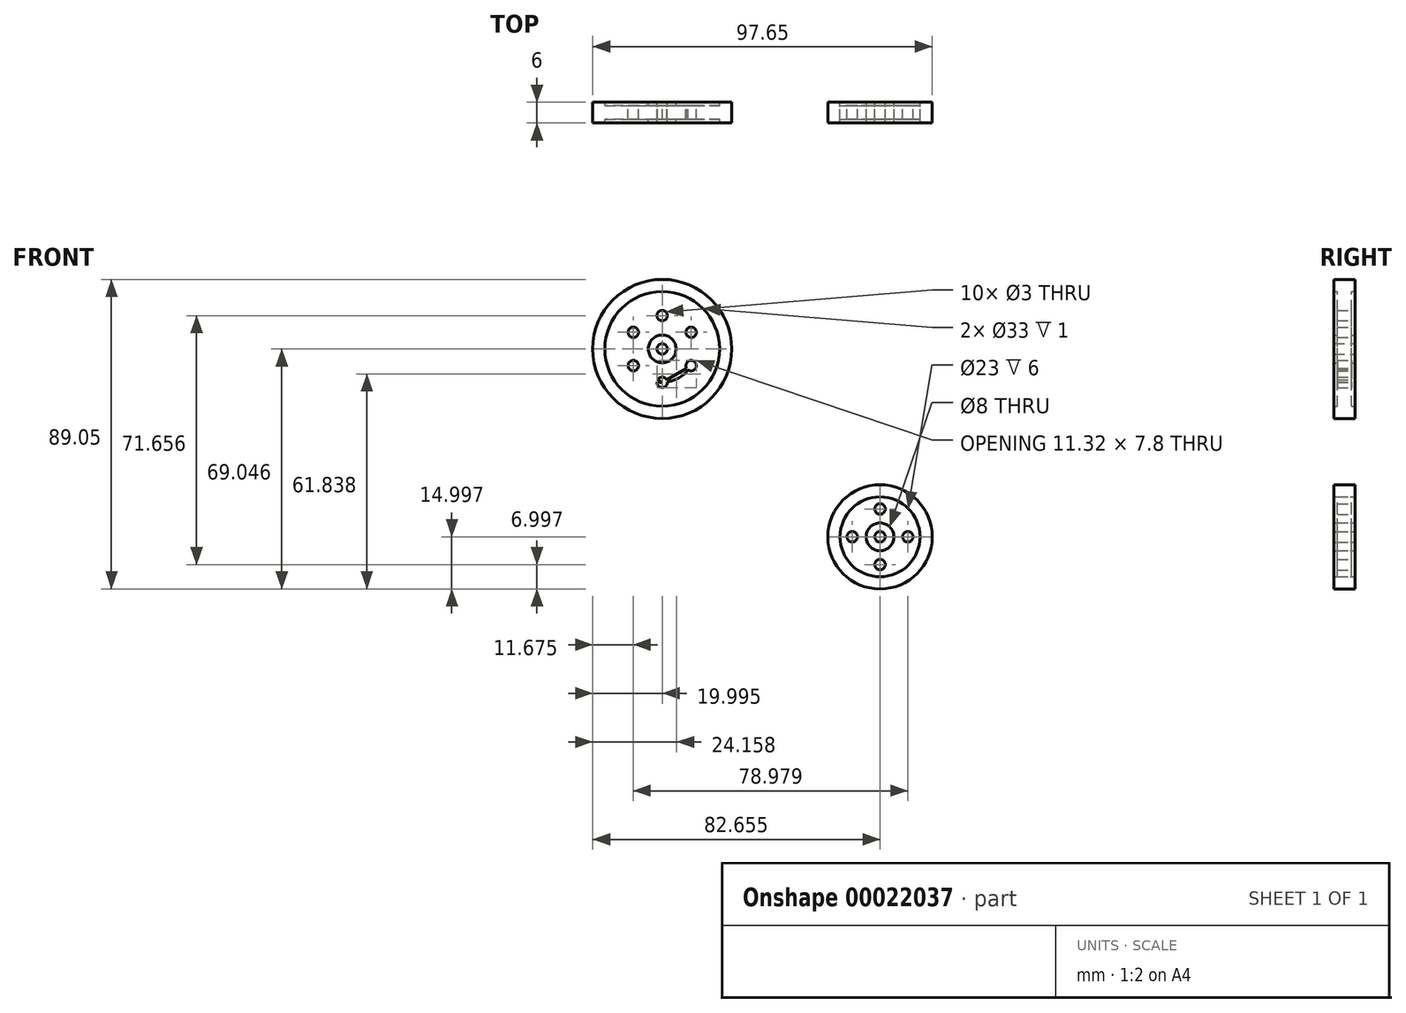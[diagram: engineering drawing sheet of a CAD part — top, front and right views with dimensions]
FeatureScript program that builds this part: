
annotation { "Feature Type Name" : "Feature", "Feature Type Description" : "" }
export const myFeature = defineFeature(function(context is Context, id is Id, definition is map)
    precondition{}
    {
        {
            var Q0;
            Q0=qCreatedBy(makeId("Front.planeOp"),FACE);
            var sketch = newSketch(context, id + "F0", { "sketchPlane" : qUnion([Q0])});
            skCircle(sketch, "E0", {"center": v(-77.4, 40.17) * mm, "radius": 20 * mm});
            skCircle(sketch, "E1", {"center": v(-77.4, 40.17) * mm, "radius": 4 * mm});
            skCircle(sketch, "E2", {"center": v(-77.4, 40.17) * mm, "radius": 9.6 * mm});
            skCircle(sketch, "E3.cCircle", {"center": v(-77.4, 40.17) * mm, "radius": 9.6 * mm, "construction": true});
            skLineSegment(sketch, "E3.0", {"start": v(-77.4, 30.56) * mm, "end": v(-85.72, 35.36) * mm});
            skLineSegment(sketch, "E3.1", {"start": v(-85.72, 35.36) * mm, "end": v(-85.72, 44.97) * mm});
            skLineSegment(sketch, "E3.2", {"start": v(-85.72, 44.97) * mm, "end": v(-77.4, 49.77) * mm});
            skLineSegment(sketch, "E3.3", {"start": v(-77.4, 49.77) * mm, "end": v(-69.08, 44.97) * mm});
            skLineSegment(sketch, "E3.4", {"start": v(-69.08, 44.97) * mm, "end": v(-69.08, 35.36) * mm});
            skLineSegment(sketch, "E3.5", {"start": v(-69.08, 35.36) * mm, "end": v(-77.4, 30.56) * mm});
            skCircle(sketch, "E4", {"center": v(-77.4, 49.77) * mm, "radius": 1.5 * mm});
            skCircle(sketch, "E5", {"center": v(-69.08, 44.97) * mm, "radius": 1.5 * mm});
            skCircle(sketch, "E6", {"center": v(-69.08, 35.36) * mm, "radius": 1.5 * mm});
            skCircle(sketch, "E7", {"center": v(-77.4, 30.56) * mm, "radius": 1.5 * mm});
            skCircle(sketch, "E8", {"center": v(-85.72, 35.36) * mm, "radius": 1.5 * mm});
            skCircle(sketch, "E9", {"center": v(-85.72, 44.97) * mm, "radius": 1.5 * mm});
            skCircle(sketch, "E10", {"center": v(-77.4, 40.17) * mm, "radius": 1.5 * mm});
            skCircle(sketch, "E11", {"center": v(-77.4, 40.17) * mm, "radius": 16.5 * mm});
            skSolve(sketch);
        }
        {
            var Q0;
            Q0=makeQuery(id+"F0.imprint","IMPRINT",FACE,{"disambiguationData":[TD([[makeQuery(id+"F0.imprint","IMPRINT",EDGE,{"derivedFrom":sQuery(id+"F0.wireOp",EDGE,"E0")}),1.0]])]});
            extrude(context, id + "F1", {"entities" : qUnion([Q0]), "endBound" : BoundingType.SYMMETRIC, "depth" : 6 * mm});
        }
        {
            var Q0;
            Q0=makeQuery(id+"F0.imprint","IMPRINT",FACE,{"disambiguationData":[TD([[makeQuery(id+"F0.imprint","IMPRINT",EDGE,{"derivedFrom":sQuery(id+"F0.wireOp",EDGE,"E11")}),1.0]])]});
            extrude(context, id + "F2", {"entities" : qUnion([Q0]), "operationType" : NewBodyOperationType.ADD, "endBound" : BoundingType.SYMMETRIC, "depth" : 4 * mm});
        }
        {
            var Q0;
            {var subQ0=sQuery(id+"F0.wireOp",EDGE,"E9");var subQ3=sQuery(id+"F0.wireOp",EDGE,"E2");var subQ4=makeQuery(id+"F0.imprint","INTERSECT",VERTEX,{"disambiguationData":[OD(1.0)],"derivedFrom":[subQ3,subQ0]});Q0=makeQuery(id+"F0.imprint","IMPRINT",FACE,{"disambiguationData":[TD([[makeQuery(id+"F0.imprint","IMPRINT",EDGE,{"disambiguationData":[TD([[subQ4,-1.0]])],"derivedFrom":subQ3}),1.0]])]});}
            var Q1;
            Q1=makeQuery(id+"F0.imprint","IMPRINT",FACE,{"disambiguationData":[TD([[makeQuery(id+"F0.imprint","IMPRINT",EDGE,{"derivedFrom":sQuery(id+"F0.wireOp",EDGE,"E1")}),-1.0]])]});
            var Q2;
            {var subQ3=sQuery(id+"F0.wireOp",EDGE,"E2");var subQ5=sQuery(id+"F0.wireOp",EDGE,"E4");var subQ7=makeQuery(id+"F0.imprint","INTERSECT",VERTEX,{"disambiguationData":[OD(1.0)],"derivedFrom":[subQ3,subQ5]});Q2=makeQuery(id+"F0.imprint","IMPRINT",FACE,{"disambiguationData":[TD([[makeQuery(id+"F0.imprint","IMPRINT",EDGE,{"disambiguationData":[TD([[subQ7,-1.0]])],"derivedFrom":subQ3}),1.0]])]});}
            var Q3;
            {var subQ3=sQuery(id+"F0.wireOp",EDGE,"E2");var subQ5=sQuery(id+"F0.wireOp",EDGE,"E8");var subQ7=makeQuery(id+"F0.imprint","INTERSECT",VERTEX,{"disambiguationData":[OD(1.0)],"derivedFrom":[subQ3,subQ5]});Q3=makeQuery(id+"F0.imprint","IMPRINT",FACE,{"disambiguationData":[TD([[makeQuery(id+"F0.imprint","IMPRINT",EDGE,{"disambiguationData":[TD([[subQ7,-1.0]])],"derivedFrom":subQ3}),1.0]])]});}
            var Q4;
            {var subQ0=sQuery(id+"F0.wireOp",EDGE,"E7");var subQ3=sQuery(id+"F0.wireOp",EDGE,"E2");var subQ4=makeQuery(id+"F0.imprint","INTERSECT",VERTEX,{"disambiguationData":[OD(1.0)],"derivedFrom":[subQ3,subQ0]});Q4=makeQuery(id+"F0.imprint","IMPRINT",FACE,{"disambiguationData":[TD([[makeQuery(id+"F0.imprint","IMPRINT",EDGE,{"disambiguationData":[TD([[subQ4,-1.0]])],"derivedFrom":subQ3}),1.0]])]});}
            var Q5;
            {var subQ3=sQuery(id+"F0.wireOp",EDGE,"E2");var subQ5=sQuery(id+"F0.wireOp",EDGE,"E5");var subQ7=makeQuery(id+"F0.imprint","INTERSECT",VERTEX,{"disambiguationData":[OD(0.0)],"derivedFrom":[subQ3,subQ5]});Q5=makeQuery(id+"F0.imprint","IMPRINT",FACE,{"disambiguationData":[TD([[makeQuery(id+"F0.imprint","IMPRINT",EDGE,{"disambiguationData":[TD([[subQ7,1.0]])],"derivedFrom":subQ3}),1.0]])]});}
            var Q6;
            {var subQ0=sQuery(id+"F0.wireOp",EDGE,"E5");var subQ3=sQuery(id+"F0.wireOp",EDGE,"E2");var subQ4=makeQuery(id+"F0.imprint","INTERSECT",VERTEX,{"disambiguationData":[OD(1.0)],"derivedFrom":[subQ3,subQ0]});Q6=makeQuery(id+"F0.imprint","IMPRINT",FACE,{"disambiguationData":[TD([[makeQuery(id+"F0.imprint","IMPRINT",EDGE,{"disambiguationData":[TD([[subQ4,-1.0]])],"derivedFrom":subQ3}),1.0]])]});}
            extrude(context, id + "F3", {"entities" : qUnion([Q0, Q1, Q2, Q3, Q4, Q5, Q6]), "operationType" : NewBodyOperationType.ADD, "endBound" : BoundingType.SYMMETRIC, "depth" : 4 * mm});
        }
        {
            var Q0;
            Q0=makeQuery(id+"F0.imprint","IMPRINT",FACE,{"disambiguationData":[TD([[makeQuery(id+"F0.imprint","IMPRINT",EDGE,{"derivedFrom":sQuery(id+"F0.wireOp",EDGE,"E1")}),1.0]])]});
            extrude(context, id + "F4", {"entities" : qUnion([Q0]), "operationType" : NewBodyOperationType.ADD, "endBound" : BoundingType.SYMMETRIC, "depth" : 6 * mm});
        }
        {
            var Q0;
            Q0=qCreatedBy(makeId("Front.planeOp"),FACE);
            var sketch = newSketch(context, id + "F5", { "sketchPlane" : qUnion([Q0])});
            skCircle(sketch, "E12", {"center": v(-14.75, -13.88) * mm, "radius": 15 * mm});
            skCircle(sketch, "E13", {"center": v(-14.75, -13.88) * mm, "radius": 4 * mm});
            skCircle(sketch, "E14", {"center": v(-14.75, -21.88) * mm, "radius": 1.5 * mm});
            skCircle(sketch, "E15", {"center": v(-14.75, -13.88) * mm, "radius": 1.5 * mm});
            skCircle(sketch, "E16", {"center": v(-14.75, -13.88) * mm, "radius": 11.5 * mm});
            skCircle(sketch, "E17.1.0", {"center": v(-6.75, -13.88) * mm, "radius": 1.5 * mm});
            skCircle(sketch, "E17.2.0", {"center": v(-14.75, -5.88) * mm, "radius": 1.5 * mm});
            skCircle(sketch, "E17.3.0", {"center": v(-22.75, -13.88) * mm, "radius": 1.5 * mm});
            skSolve(sketch);
        }
        {
            var Q0;
            Q0=makeQuery(id+"F5.imprint","IMPRINT",FACE,{"disambiguationData":[TD([[makeQuery(id+"F5.imprint","IMPRINT",EDGE,{"derivedFrom":sQuery(id+"F5.wireOp",EDGE,"E12")}),1.0]])]});
            var Q1;
            Q1=makeQuery(id+"F5.imprint","IMPRINT",FACE,{"disambiguationData":[TD([[makeQuery(id+"F5.imprint","IMPRINT",EDGE,{"derivedFrom":sQuery(id+"F5.wireOp",EDGE,"E13")}),1.0]])]});
            extrude(context, id + "F6", {"entities" : qUnion([Q0, Q1]), "endBound" : BoundingType.SYMMETRIC, "depth" : 6 * mm});
        }
        {
            var Q0;
            Q0=makeQuery(id+"F5.imprint","IMPRINT",FACE,{"disambiguationData":[TD([[makeQuery(id+"F5.imprint","IMPRINT",EDGE,{"derivedFrom":sQuery(id+"F5.wireOp",EDGE,"E13")}),-1.0]])]});
            extrude(context, id + "F7", {"entities" : qUnion([Q0]), "endBound" : BoundingType.SYMMETRIC, "depth" : 4 * mm});
        }
    });
